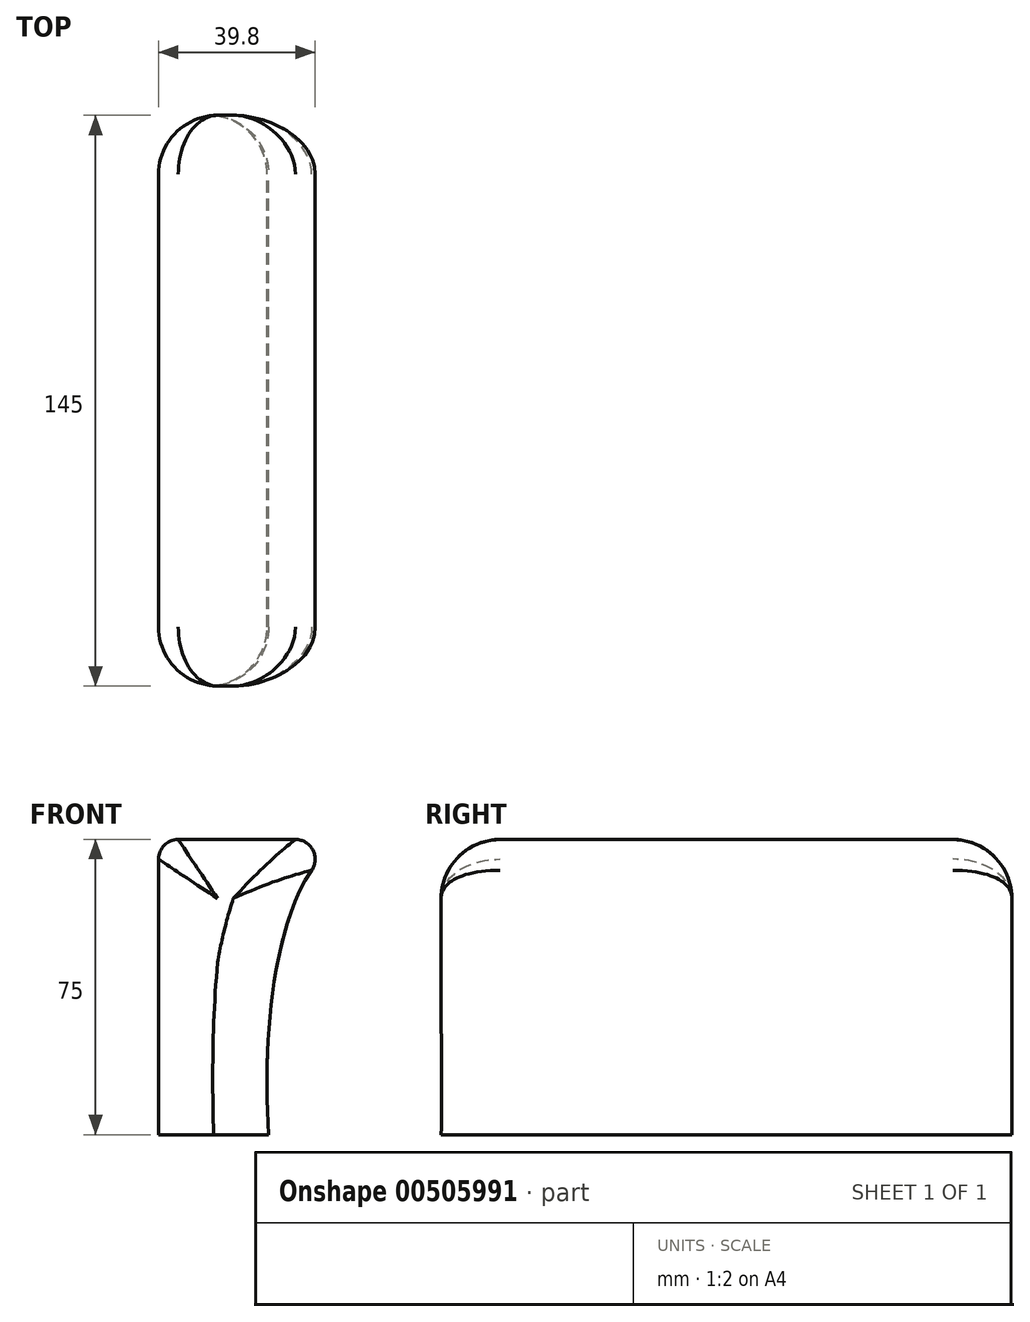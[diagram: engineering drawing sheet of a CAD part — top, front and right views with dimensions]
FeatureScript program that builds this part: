
annotation { "Feature Type Name" : "Feature", "Feature Type Description" : "" }
export const myFeature = defineFeature(function(context is Context, id is Id, definition is map)
    precondition{}
    {
        {
            var Q0;
            Q0=qCreatedBy(makeId("Front.planeOp"),FACE);
            var sketch = newSketch(context, id + "F0", { "sketchPlane" : qUnion([Q0])});
            skLineSegment(sketch, "E0", {"start": v(-26.38, 0) * mm, "end": v(-26.38, 70) * mm});
            skLineSegment(sketch, "E1", {"start": v(-21.38, 75) * mm, "end": v(8.42, 75) * mm});
            skFitSpline(sketch, "E2", {"points": [v(1.62, 0) * mm, v(6.3, 53.53) * mm, v(11.73, 65.95) * mm, v(20.62, 75) * mm], "startDerivative": vector(-9.64, 157.33) * mm, "endDerivative": vector(46.08, 26.81) * mm});
            skLineSegment(sketch, "E3", {"start": v(-26.38, 0) * mm, "end": v(1.62, 0) * mm});
            skArc(sketch, "E4.filletArc", {"start": v(12.52, 67.15) * mm, "mid": v(12.85, 72.32) * mm, "end": v(8.42, 75) * mm});
            skPoint(sketch, "E5.visualSharp", {"position": v(-26.38, 75) * mm});
            skArc(sketch, "E5.filletArc", {"start": v(-21.38, 75) * mm, "mid": v(-24.92, 73.54) * mm, "end": v(-26.38, 70) * mm});
            skSolve(sketch);
        }
        {
            var Q0;
            Q0 = qSketchRegion(id + "F0", true);
            extrude(context, id + "F1", {"entities" : qUnion([Q0]), "depth" : 145 * mm, "offsetDistance" : 25 * mm});
        }
        {
            var Q0;
            Q0=makeQuery(id+"F1.opExtrude","CAP_EDGE",EDGE,{"disambiguationData":[OSD([sQuery(id+"F0.wireOp",EDGE,"E1")])],"isStart":false});
            var Q1;
            Q1=makeQuery(id+"F1.opExtrude","CAP_EDGE",EDGE,{"disambiguationData":[OSD([sQuery(id+"F0.wireOp",EDGE,"E1")])],"isStart":true});
            fillet(context, id + "F2", {"entities" : qUnion([Q0, Q1]), "radius" : 15 * mm, "tangentPropagation" : true, "allowEdgeOverflow" : false});
        }
    });
